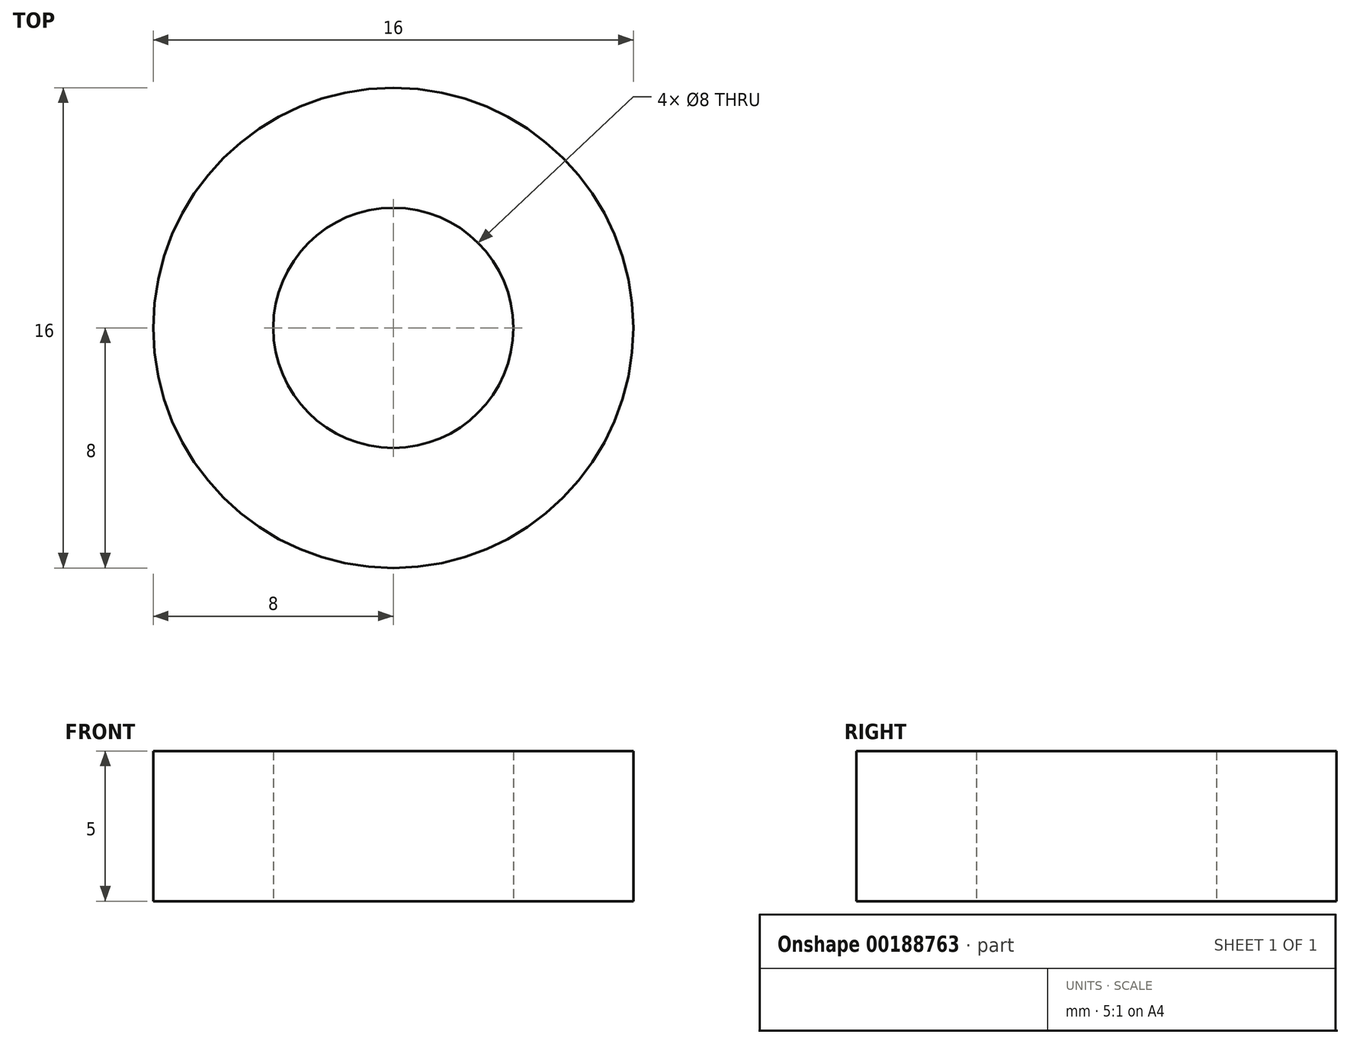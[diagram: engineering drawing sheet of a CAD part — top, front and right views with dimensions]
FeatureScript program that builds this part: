
annotation { "Feature Type Name" : "Feature", "Feature Type Description" : "" }
export const myFeature = defineFeature(function(context is Context, id is Id, definition is map)
    precondition{}
    {
        {
            var Q0;
            Q0=qCreatedBy(makeId("Top.planeOp"),FACE);
            var sketch = newSketch(context, id + "F0", { "sketchPlane" : qUnion([Q0])});
            skCircle(sketch, "E0", {"center": v(0, 0) * mm, "radius": 8 * mm});
            skCircle(sketch, "E1", {"center": v(0, 0) * mm, "radius": 4 * mm});
            skSolve(sketch);
        }
        {
            var Q0;
            Q0=makeQuery(id+"F0.imprint","IMPRINT",FACE,{"disambiguationData":[TD([[makeQuery(id+"F0.imprint","IMPRINT",EDGE,{"derivedFrom":sQuery(id+"F0.wireOp",EDGE,"E0")}),1.0]])]});
            extrude(context, id + "F1", {"entities" : qUnion([Q0]), "depth" : 5 * mm, "offsetDistance" : 25 * mm});
        }
    });
